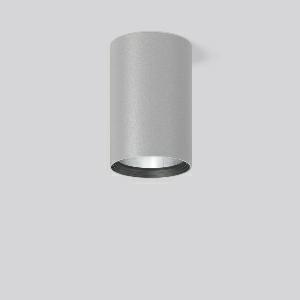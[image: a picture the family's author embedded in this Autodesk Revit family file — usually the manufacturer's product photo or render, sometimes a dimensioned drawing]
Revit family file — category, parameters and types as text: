
# Revit family: heledon_maxi_a_931247_004_2_67e4
name_source: partatom
category: Lighting Fixtures
units: mm (PartAtom-declared; Revit-internal decimal feet)

## family parameters
Cut with Voids When Loaded = No
Host = Face
Light Source = No
Part Type = Normal
Room Calculation Point = No
Round Connector Dimension = Use Diameter
Shared = No

## types (1)
- HELEDON maxi A (1 x LED Modul 927 bakery, 3300 lm, 2700)
    Apparent Load = 33 VA
    Approval mark = CE
    CIE Flux Codes = 96 100 100 100 100
    Color Rendering = 90
    Color Temperature = 2700
    Default Elevation = 1800 mm
    Description = Series: HELEDON maxi
Cylindrical surface-mounted downlight. Housing: die-cast aluminium, powder-coated. Internal ceiling frame polycarbonate with bayonet mounting. Black plastic ring and recessed LED to prevent glare from the side. Optical assembly with reflector made of MIRO-Silver with 98% total light reflection for outstanding efficiency - can be changed without tools. Special LED for illumination of pastries included. Suitable for Ceiling mounting. Easy installation with a separate ceiling frame with bayonet mounting and plug connection. Driver integrated. Connected via plug-in connector. High quality converter without flickering and stroboscopic effect. The following accessories can be mounted without use of tools: interchangeable lenses, decorative glasses, honeycomb louvre, clear and frosted diffusers, white interchangeable plastic ring. 
Colour: silver
Diameter: 123 mm
Height: 183 mm
Lamp: LED
Socket: without socket
Colour temperature: bakery
Colour rendering index (CRI): 97
System power: 33 W
Rated luminous flux: 3300 lm
Luminous efficiency: 100 lm/W
Control gear: Regulated power supply
Protection class: I
Type of protection: IP 20
    Height = 183 mm
    Lamp = 1 x LED Modul 927 bakery
    Lamp Light Flux = 3300 lm
    Lamp count = 1
    Length = 123 mm
    Lifetime = 50000 h
    Luminous efficacy = 100 lm/W
    Manufacturer = RZB
    ModVariant = No
    Model = 931247.004.2
    Mounting Place = Ceiling
    Mounting Type = Surface mounted
    Number of Poles = 1
    OnlyDefault = Yes
    Power Factor = 1
    Product Name = HELEDON maxi A
    Product group = Surface mounted downlights
    ProductGroupID = 302
    Protection Class = Protection class I
    Protection Degree = IP 20
    RLX_Detail_Level = 1
    RLX_Emergency_Light_Flux = 0 lm
    RLX_Emergency_Type = 0
    RLX_Emergency_Type_DB = No
    RlxData = <blob elided: 98893 chars, md5=d3d952a3>
    Socket = socket
    Standby Power = 0 W
    System Light Flux = 3300 lm
    System Power = 33 W
    Type Comments = Product without accessories
    Type Image = 931192.004.jpg
    URL = http://relux.com
    VarID = ---
    Voltage = 230 V
    Voltage Range = 220-240 V
    Weight = 0.00 kg
    Width = 0 mm  [stored 0 ft]

note: [stored X ft] marks values corroborated as IEEE doubles in the binary element streams (Revit-internal decimal feet)

## geometry (parser evidence)
native form markers: Blend x4, Sweep x9
no freeform markers — native parametric forms only
